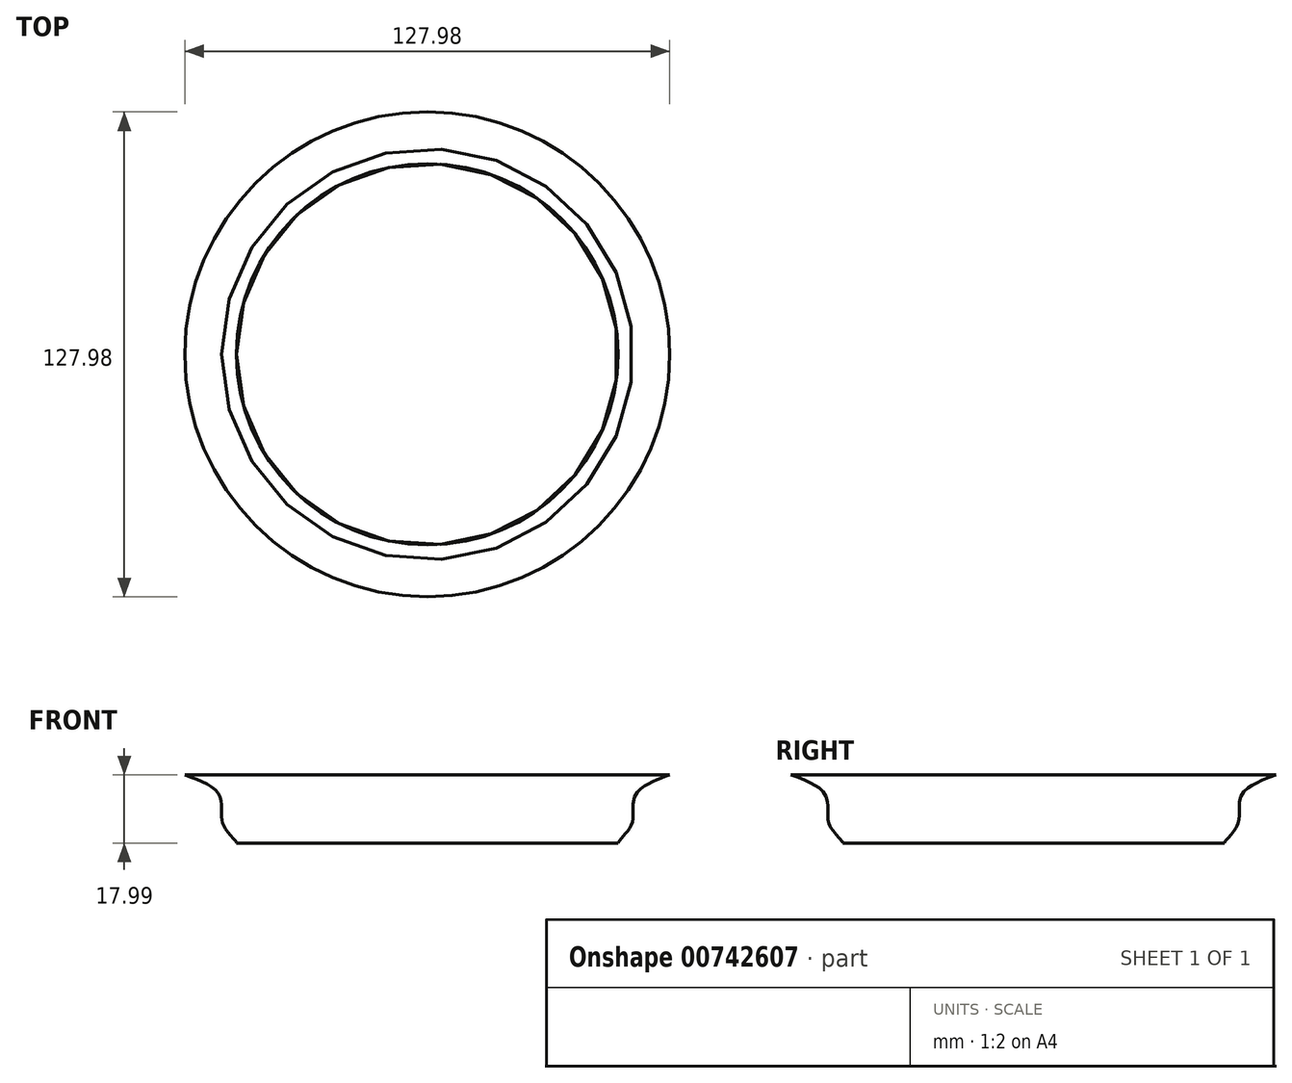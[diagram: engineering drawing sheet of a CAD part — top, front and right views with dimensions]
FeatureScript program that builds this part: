
annotation { "Feature Type Name" : "Feature", "Feature Type Description" : "" }
export const myFeature = defineFeature(function(context is Context, id is Id, definition is map)
    precondition{}
    {
        {
            var Q0;
            Q0=qCreatedBy(makeId("Front.planeOp"),FACE);
            var sketch = newSketch(context, id + "F0", { "sketchPlane" : qUnion([Q0])});
            skFitSpline(sketch, "E0", {"points": [v(-63.99, 23.7) * mm, v(-54.99, 18.49) * mm, v(-54.28, 12.73) * mm, v(-53.02, 9.07) * mm, v(-50.35, 5.84) * mm, v(-50.35, 5.7) * mm], "startDerivative": vector(35.64, -13.26) * mm, "endDerivative": vector(-1.25, -2.73) * mm});
            skLineSegment(sketch, "E1", {"start": v(0, 5.7) * mm, "end": v(-50.35, 5.7) * mm});
            skLineSegment(sketch, "E2", {"start": v(0, 23.7) * mm, "end": v(0, 5.7) * mm});
            skSolve(sketch);
        }
        {
            var Q0;
            Q0=sQuery(id+"F0.wireOp",EDGE,"E0");
            var Q1;
            Q1=sQuery(id+"F0.wireOp",EDGE,"E1");
            var Q2;
            Q2=sQuery(id+"F0.wireOp",EDGE,"E2");
            revolve(context, id + "F1", {"bodyType" : ToolBodyType.SURFACE, "surfaceOperationType" : NewSurfaceOperationType.NEW, "surfaceEntities" : qUnion([Q0, Q1]), "axis" : qUnion([Q2]), "revolveType" : RevolveType.FULL});
        }
    });
